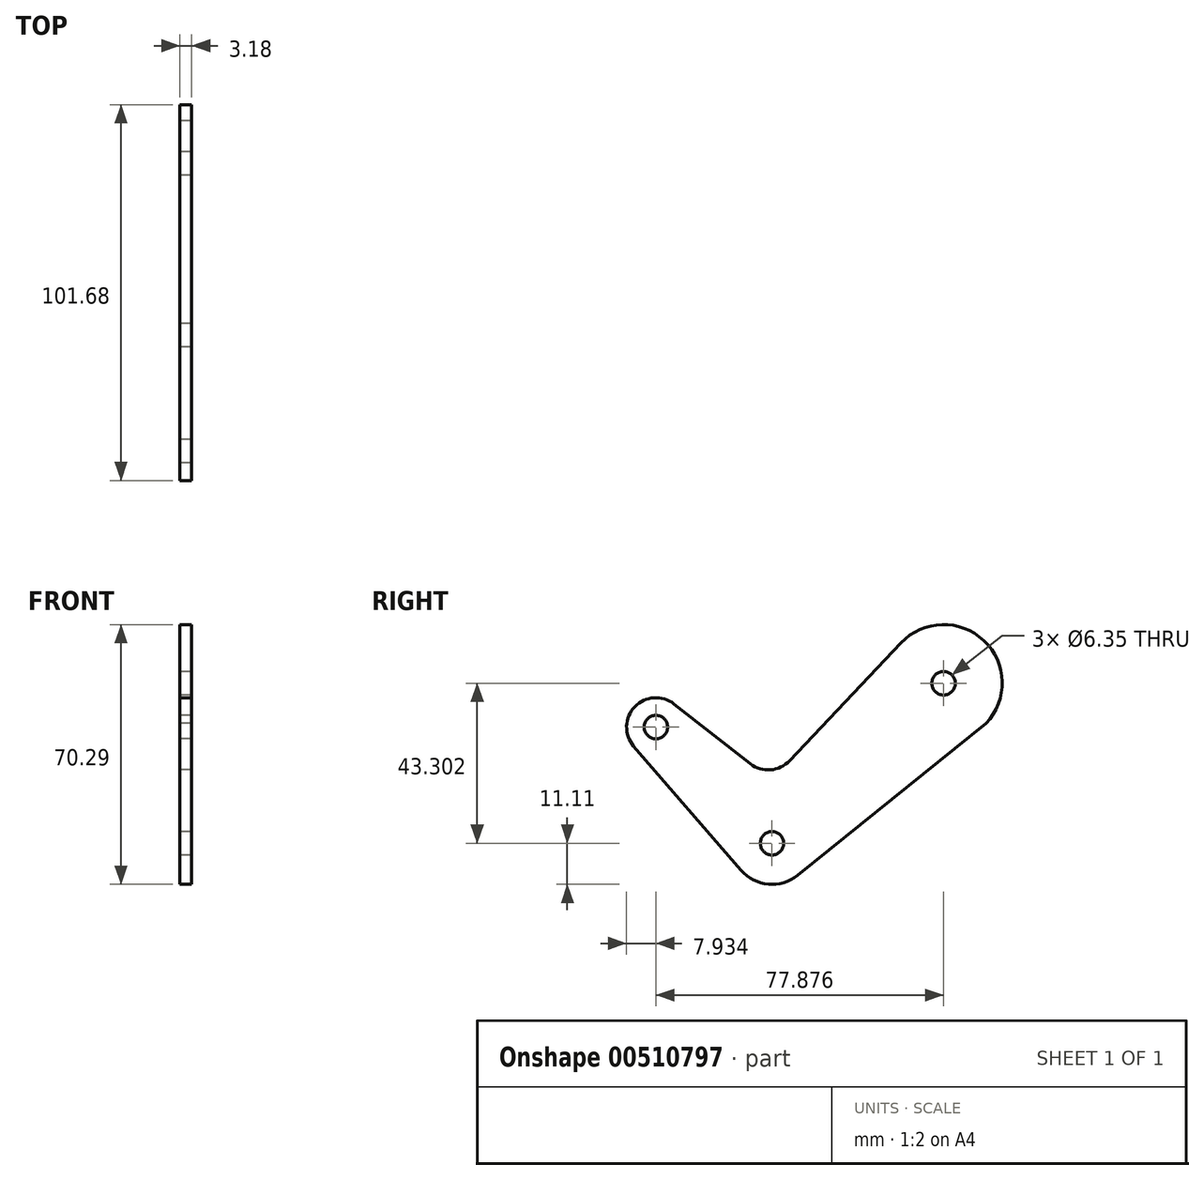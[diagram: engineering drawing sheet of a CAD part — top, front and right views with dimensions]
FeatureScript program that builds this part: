
annotation { "Feature Type Name" : "Feature", "Feature Type Description" : "" }
export const myFeature = defineFeature(function(context is Context, id is Id, definition is map)
    precondition{}
    {
        {
            var Q0;
            Q0=qCreatedBy(makeId("Right.planeOp"),FACE);
            var sketch = newSketch(context, id + "F0", { "sketchPlane" : qUnion([Q0])});
            skLineSegment(sketch, "E0", {"start": v(-26.18, -12.3) * mm, "end": v(-23.93, -14.55) * mm, "construction": true});
            skLineSegment(sketch, "E1", {"start": v(5.25, -43.74) * mm, "end": v(7.58, -41.58) * mm, "construction": true});
            skCircle(sketch, "E2", {"center": v(-26.18, -12.3) * mm, "radius": 3.18 * mm});
            skCircle(sketch, "E3", {"center": v(5.25, -43.74) * mm, "radius": 3.18 * mm});
            skCircle(sketch, "E4", {"center": v(51.7, -0.44) * mm, "radius": 3.18 * mm});
            skArc(sketch, "E5", {"start": v(-21.28, -6.06) * mm, "mid": v(-31.95, -6.86) * mm, "end": v(-32.13, -17.56) * mm});
            skArc(sketch, "E6", {"start": v(-3.14, -51.02) * mm, "mid": v(4.26, -54.8) * mm, "end": v(12.22, -52.4) * mm});
            skArc(sketch, "E7", {"start": v(59.87, -14.05) * mm, "mid": v(64.08, 9.5) * mm, "end": v(40.17, 10.47) * mm});
            skLineSegment(sketch, "E8", {"start": v(-32.22, -17.45) * mm, "end": v(-3.14, -51.02) * mm});
            skLineSegment(sketch, "E9", {"start": v(-0.68, -22.2) * mm, "end": v(-21.28, -6.06) * mm});
            skArc(sketch, "E10.filletArc", {"start": v(-0.68, -22.2) * mm, "mid": v(4.84, -23.88) * mm, "end": v(10.04, -21.37) * mm});
            skLineSegment(sketch, "E11", {"start": v(10.04, -21.37) * mm, "end": v(40.19, 10.5) * mm});
            skLineSegment(sketch, "E12", {"start": v(63.25, -11.33) * mm, "end": v(12.22, -52.4) * mm});
            skLineSegment(sketch, "E13.trimOffspring", {"start": v(3, -41.5) * mm, "end": v(5.25, -43.74) * mm, "construction": true});
            skSolve(sketch);
        }
        {
            var Q0;
            Q0=makeQuery(id+"F0.imprint","IMPRINT",FACE,{"disambiguationData":[TD([[makeQuery(id+"F0.imprint","IMPRINT",EDGE,{"derivedFrom":sQuery(id+"F0.wireOp",EDGE,"E2")}),-1.0]])]});
            extrude(context, id + "F1", {"entities" : qUnion([Q0]), "depth" : 3.17 * mm, "offsetDistance" : 25.4 * mm});
        }
    });
